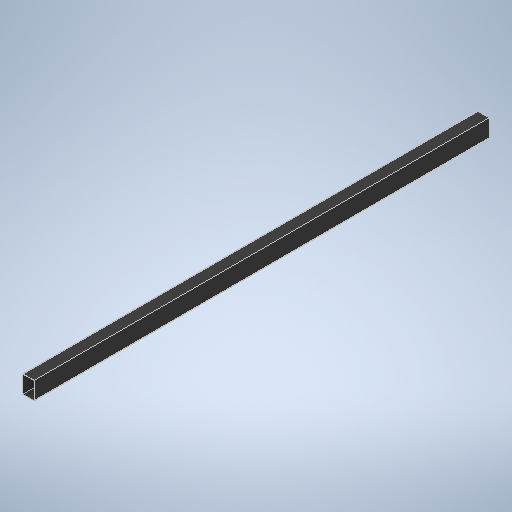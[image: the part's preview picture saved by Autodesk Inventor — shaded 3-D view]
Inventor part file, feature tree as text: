
AUTODESK INVENTOR PART (.ipt)
format: ipt  version: 2025 (Build 290162010, 162A)  size: 257,536 bytes
history: native  units: in
note: dims shown in document units (in); Inventor stores cm internally (conversion verified against a paired STEP export)
features: extrude x1, sketch x1
ambient origin geometry x8: Origin, YZ Plane, XZ Plane, XY Plane, X Axis, Y Axis, Z Axis, Center Point
bodies: Solid1 (feature_tree)
feature tree (2):
  extrude  "Extrusion1"  Depth=3.5in
  sketch  "Sketch1"  dims[d1=5.5in d2=3.5in d3=0.0625in d4=144.0in d5=0.0in]
